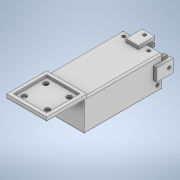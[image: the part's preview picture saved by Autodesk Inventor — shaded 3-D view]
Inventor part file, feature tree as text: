
AUTODESK INVENTOR PART (.ipt)
format: ipt  version: 2020 (Build 240168000, 168)  size: 369,664 bytes
history: native  units: in
note: dims shown in document units (in); Inventor stores cm internally (conversion verified against a paired STEP export)
features: extrude x19, sketch x19, mirror x3, fillet x2
ambient origin geometry x8: Origin, YZ Plane, XZ Plane, XY Plane, X Axis, Y Axis, Z Axis, Center Point
bodies: Solid1 (feature_tree)
feature tree (43):
  extrude  "Extrusion1"  Depth=1.8898in
  extrude  "Extrusion2"  Depth=0.1575in
  mirror  "Mirror1"
  extrude  "Extrusion3"  Depth=0.1575in
  extrude  "Extrusion4"  Depth=0.1575in
  extrude  "Extrusion5"  Depth=0.1181in
  extrude  "Extrusion6"  Depth=0.1181in
  mirror  "Mirror2"
  extrude  "Extrusion7"  Depth=0.1575in
  mirror  "Mirror3"
  extrude  "Extrusion12"  Depth=0.1575in
  extrude  "Extrusion13"  Depth=0.1575in
  extrude  "Extrusion14"  Depth=0.2362in
  extrude  "Extrusion15"  Depth=0.2362in
  extrude  "Extrusion16"  Depth=0.1575in TaperAngle=0.0deg
  extrude  "Extrusion17"  Depth=0.1575in
  extrude  "Extrusion18"  Depth=0.315in
  extrude  "Extrusion19"  Depth=0.315in
  extrude  "Extrusion20"  Depth=0.1575in
  extrude  "Extrusion21"  Depth=0.7087in
  extrude  "Extrusion22"  Depth=0.1969in
  extrude  "Extrusion23"  Depth=1.2205in
  fillet  "Fillet1"  Radius=0.7874in
  fillet  "Fillet2"  Radius=3.937in
  sketch  "Sketch1"  dims[d0=1.8898in d1=10.8661in]
  sketch  "Sketch2"  dims[d2=0.1181in d3=0.0in d4=0.1575in]
  sketch  "Sketch3"  dims[d5=1.8898in d6=0.1575in]
  sketch  "Sketch4"  dims[d7=0.1575in d8=0.1575in]
  sketch  "Sketch5"  dims[d9=0.1181in d10=0.0in d11=0.1181in]
  sketch  "Sketch6"  dims[d12=0.1181in d13=0.1181in]
  sketch  "Sketch7"  dims[d14=1.378in d15=0.0in d16=0.1575in]
  sketch  "Sketch12"  dims[d17=0.315in d18=0.0in d19=0.1575in]
  sketch  "Sketch13"  dims[d20=0.1575in d21=0.0in d22=0.1575in]
  sketch  "Sketch14"  dims[d23=0.1575in d24=0.0in d25=0.2362in]
  sketch  "Sketch15"  dims[d26=0.2362in d27=0.2362in]
  sketch  "Sketch16"  dims[d28=0.2362in d29=0.1575in d30=0.0in]
  sketch  "Sketch17"  dims[d53=0.1575in d54=0.1575in]
  sketch  "Sketch18"  dims[d55=1.378in d56=0.0in d57=0.315in]
  sketch  "Sketch19"  dims[d58=0.1181in d59=0.0in d60=0.315in]
  sketch  "Sketch20"  dims[d61=0.1181in d62=0.0in d63=0.1575in]
  sketch  "Sketch21"  dims[d64=1.1811in d65=0.0in d66=0.7087in]
  sketch  "Sketch22"  dims[d67=0.1969in d68=0.1969in]
  sketch  "Sketch23"  dims[d69=0.7874in d70=0.0in d71=1.2205in d72=0.7874in d73=0.0in d74=3.937in d75=0.0in d76=0.5906in d77=0.7874in d78=0.1575in d79=0.2756in d80=0.0in d81=0.0in d82=0.7874in d83=0.5906in d84=0.1575in d85=0.2756in d86=0.0in d87=0.0in d88=0.1575in d89=0.1575in d90=0.1575in d91=0.7874in d92=0.0in d93=0.1575in d94=0.1575in d95=0.7874in d96=0.0in d97=0.3937in d98=0.0in d99=0.0787in d100=0.1575in d101=0.2362in d102=0.2756in d103=0.2362in d104=0.2756in d105=0.2362in d106=0.2756in d107=0.2362in d108=0.2756in]
